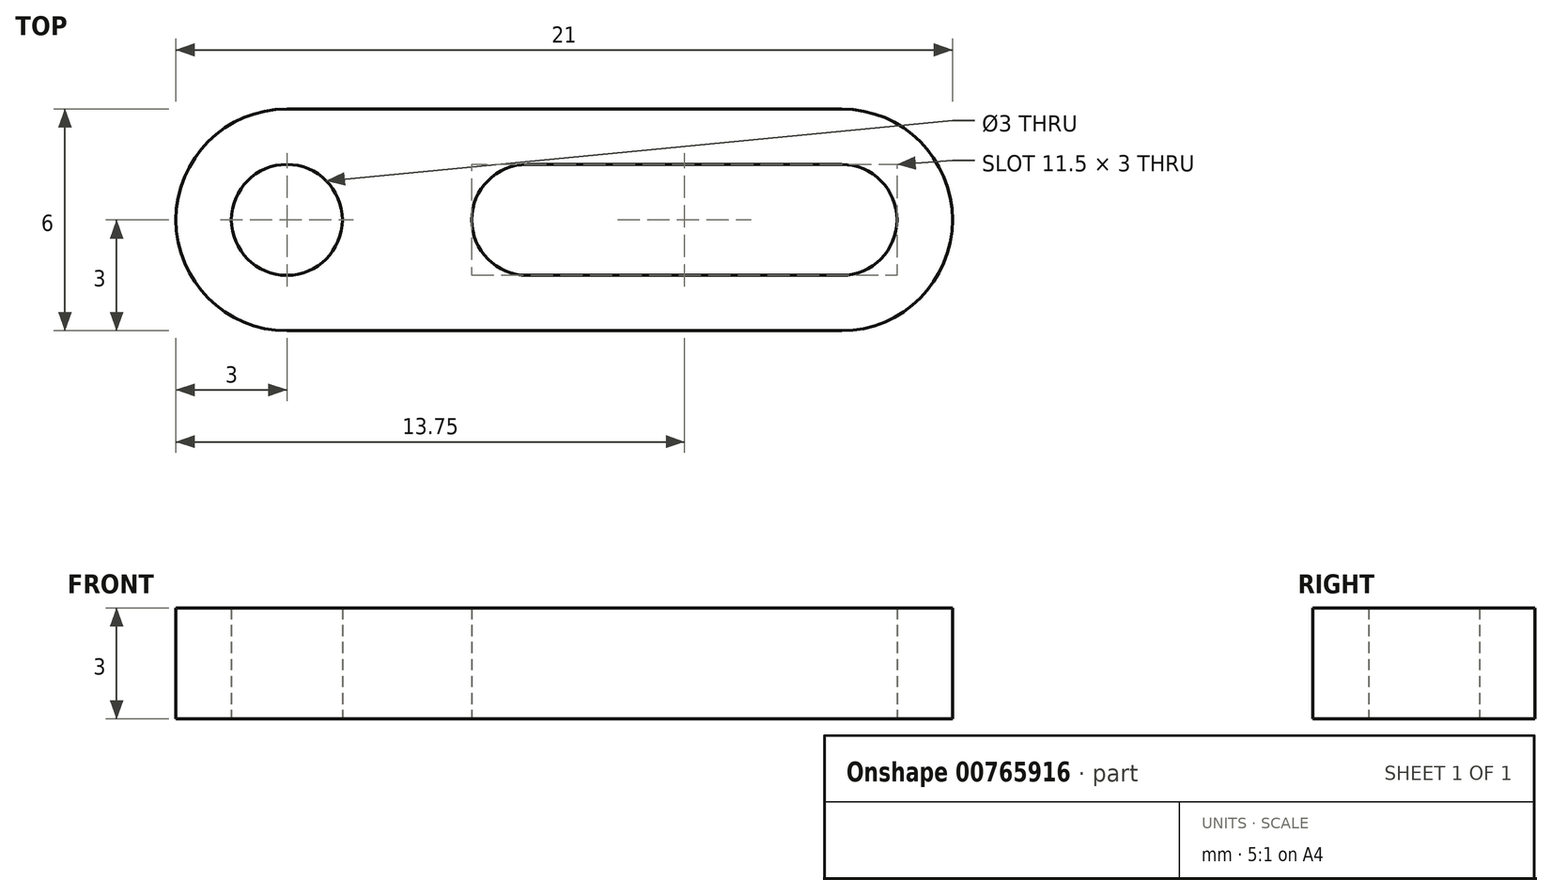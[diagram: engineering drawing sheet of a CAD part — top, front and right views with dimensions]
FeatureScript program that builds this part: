
annotation { "Feature Type Name" : "Feature", "Feature Type Description" : "" }
export const myFeature = defineFeature(function(context is Context, id is Id, definition is map)
    precondition{}
    {
        {
            var Q0;
            Q0=qCreatedBy(makeId("Top.planeOp"),FACE);
            var sketch = newSketch(context, id + "F0", { "sketchPlane" : qUnion([Q0])});
            skLineSegment(sketch, "E0", {"start": v(0, 0) * mm, "end": v(0, 26.48) * mm, "construction": true});
            skLineSegment(sketch, "E1", {"start": v(0, 3) * mm, "end": v(-7.5, 3) * mm});
            skCircle(sketch, "E2", {"center": v(-7.5, 0) * mm, "radius": 1.5 * mm});
            skCircle(sketch, "E3", {"center": v(-7.5, 0) * mm, "radius": 3 * mm});
            skCircle(sketch, "E4", {"center": v(-1, 0) * mm, "radius": 1.5 * mm});
            skLineSegment(sketch, "E5", {"start": v(-7.5, -3) * mm, "end": v(0, -3) * mm});
            skLineSegment(sketch, "E6.MirrorCS", {"start": v(7.5, -3) * mm, "end": v(0, -3) * mm});
            skCircle(sketch, "E7.MirrorC", {"center": v(7.5, 0) * mm, "radius": 1.5 * mm});
            skLineSegment(sketch, "E8.MirrorCS", {"start": v(0, 3) * mm, "end": v(7.5, 3) * mm});
            skArc(sketch, "E9", {"start": v(7.5, 3) * mm, "mid": v(10.5, 0) * mm, "end": v(7.5, -3) * mm});
            skLineSegment(sketch, "E10", {"start": v(-1, 1.5) * mm, "end": v(7.5, 1.5) * mm});
            skLineSegment(sketch, "E11", {"start": v(7.5, -1.5) * mm, "end": v(-1, -1.5) * mm});
            skSolve(sketch);
        }
        {
            var Q0;
            {var subQ5=sQuery(id+"F0.wireOp",EDGE,"E1");Q0=makeQuery(id+"F0.imprint","IMPRINT",FACE,{"disambiguationData":[TD([[makeQuery(id+"F0.imprint","IMPRINT",EDGE,{"derivedFrom":subQ5}),1.0]])]});}
            var Q1;
            Q1=makeQuery(id+"F0.imprint","IMPRINT",FACE,{"disambiguationData":[TD([[makeQuery(id+"F0.imprint","IMPRINT",EDGE,{"derivedFrom":sQuery(id+"F0.wireOp",EDGE,"E2")}),-1.0]])]});
            extrude(context, id + "F1", {"entities" : qUnion([Q0, Q1]), "depth" : 3 * mm, "offsetDistance" : 25 * mm});
        }
    });
